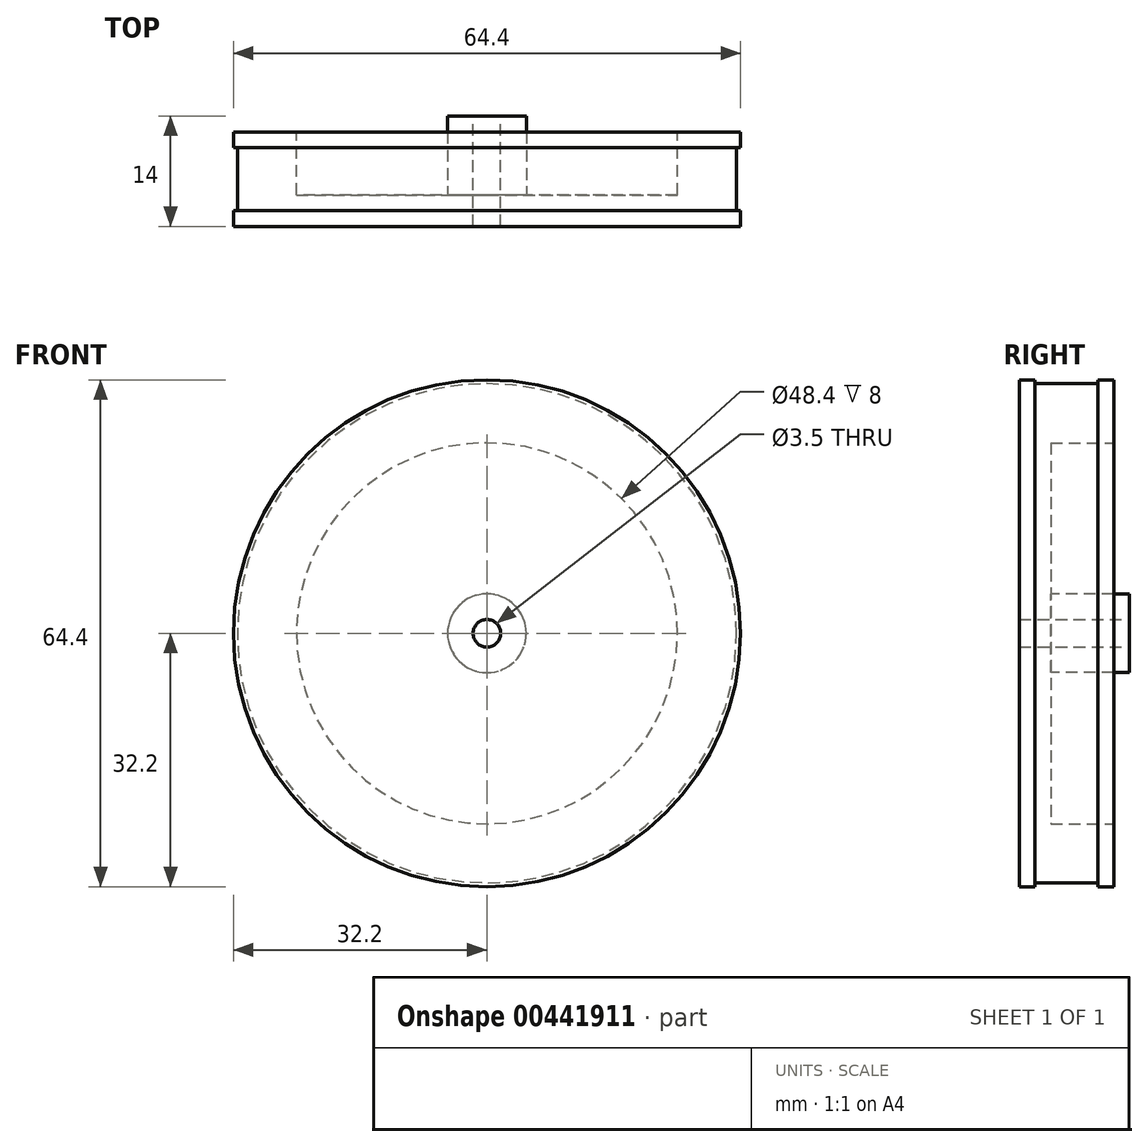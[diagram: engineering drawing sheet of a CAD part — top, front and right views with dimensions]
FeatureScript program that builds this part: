
annotation { "Feature Type Name" : "Feature", "Feature Type Description" : "" }
export const myFeature = defineFeature(function(context is Context, id is Id, definition is map)
    precondition{}
    {
        {
            var Q0;
            Q0=qCreatedBy(makeId("Top.planeOp"),FACE);
            var sketch = newSketch(context, id + "F0", { "sketchPlane" : qUnion([Q0])});
            skLineSegment(sketch, "E0", {"start": v(0, 0) * mm, "end": v(32.2, 0) * mm});
            skLineSegment(sketch, "E1", {"start": v(32.2, 0) * mm, "end": v(32.2, 2) * mm});
            skLineSegment(sketch, "E2", {"start": v(32.2, 2) * mm, "end": v(31.7, 2) * mm});
            skLineSegment(sketch, "E3", {"start": v(31.7, 2) * mm, "end": v(31.7, 10) * mm});
            skLineSegment(sketch, "E4", {"start": v(31.7, 10) * mm, "end": v(32.2, 10) * mm});
            skLineSegment(sketch, "E5", {"start": v(32.2, 10) * mm, "end": v(32.2, 12) * mm});
            skLineSegment(sketch, "E6", {"start": v(32.2, 12) * mm, "end": v(24.2, 12) * mm});
            skLineSegment(sketch, "E7", {"start": v(24.2, 12) * mm, "end": v(24.2, 4) * mm});
            skLineSegment(sketch, "E8", {"start": v(24.2, 4) * mm, "end": v(0, 4) * mm});
            skLineSegment(sketch, "E9", {"start": v(0, 4) * mm, "end": v(0, 0) * mm});
            skSolve(sketch);
        }
        {
            var Q0;
            Q0=makeQuery(id+"F0.imprint","IMPRINT",FACE,{"disambiguationData":[TD([[makeQuery(id+"F0.imprint","IMPRINT",EDGE,{"derivedFrom":sQuery(id+"F0.wireOp",EDGE,"E0")}),1.0]])]});
            var Q1;
            Q1=sQuery(id+"F0.wireOp",EDGE,"E9");
            revolve(context, id + "F1", {"entities" : qUnion([Q0]), "axis" : qUnion([Q1]), "revolveType" : RevolveType.FULL});
        }
        {
            var Q0;
            Q0=makeQuery(id+"F1.opRevolve","SWEPT_FACE",FACE,{"disambiguationData":[OSD([sQuery(id+"F0.wireOp",EDGE,"E8")])]});
            var sketch = newSketch(context, id + "F2", { "sketchPlane" : qUnion([Q0])});
            skCircle(sketch, "E10", {"center": v(0, 0) * mm, "radius": 5 * mm});
            skSolve(sketch);
        }
        {
            var Q0;
            Q0 = qSketchRegion(id + "F2", true);
            extrude(context, id + "F3", {"entities" : qUnion([Q0]), "operationType" : NewBodyOperationType.ADD, "depth" : 10 * mm});
        }
        {
            var Q0;
            Q0=makeQuery(id+"F3.opExtrude","CAP_FACE",FACE,{"disambiguationData":[OSD([sQuery(id+"F2.wireOp",EDGE,"E10")])],"isStart":false});
            var sketch = newSketch(context, id + "F4", { "sketchPlane" : qUnion([Q0])});
            skCircle(sketch, "E11.0", {"center": v(0, 0) * mm, "radius": 5 * mm});
            skCircle(sketch, "E12", {"center": v(0, 0) * mm, "radius": 1.75 * mm});
            skSolve(sketch);
        }
        {
            var Q0;
            Q0=makeQuery(id+"F4.imprint","IMPRINT",FACE,{"disambiguationData":[TD([[makeQuery(id+"F4.imprint","IMPRINT",EDGE,{"derivedFrom":sQuery(id+"F4.wireOp",EDGE,"E12")}),1.0]])]});
            extrude(context, id + "F5", {"entities" : qUnion([Q0]), "operationType" : NewBodyOperationType.REMOVE, "oppositeDirection" : true, "depth" : 25 * mm});
        }
    });
